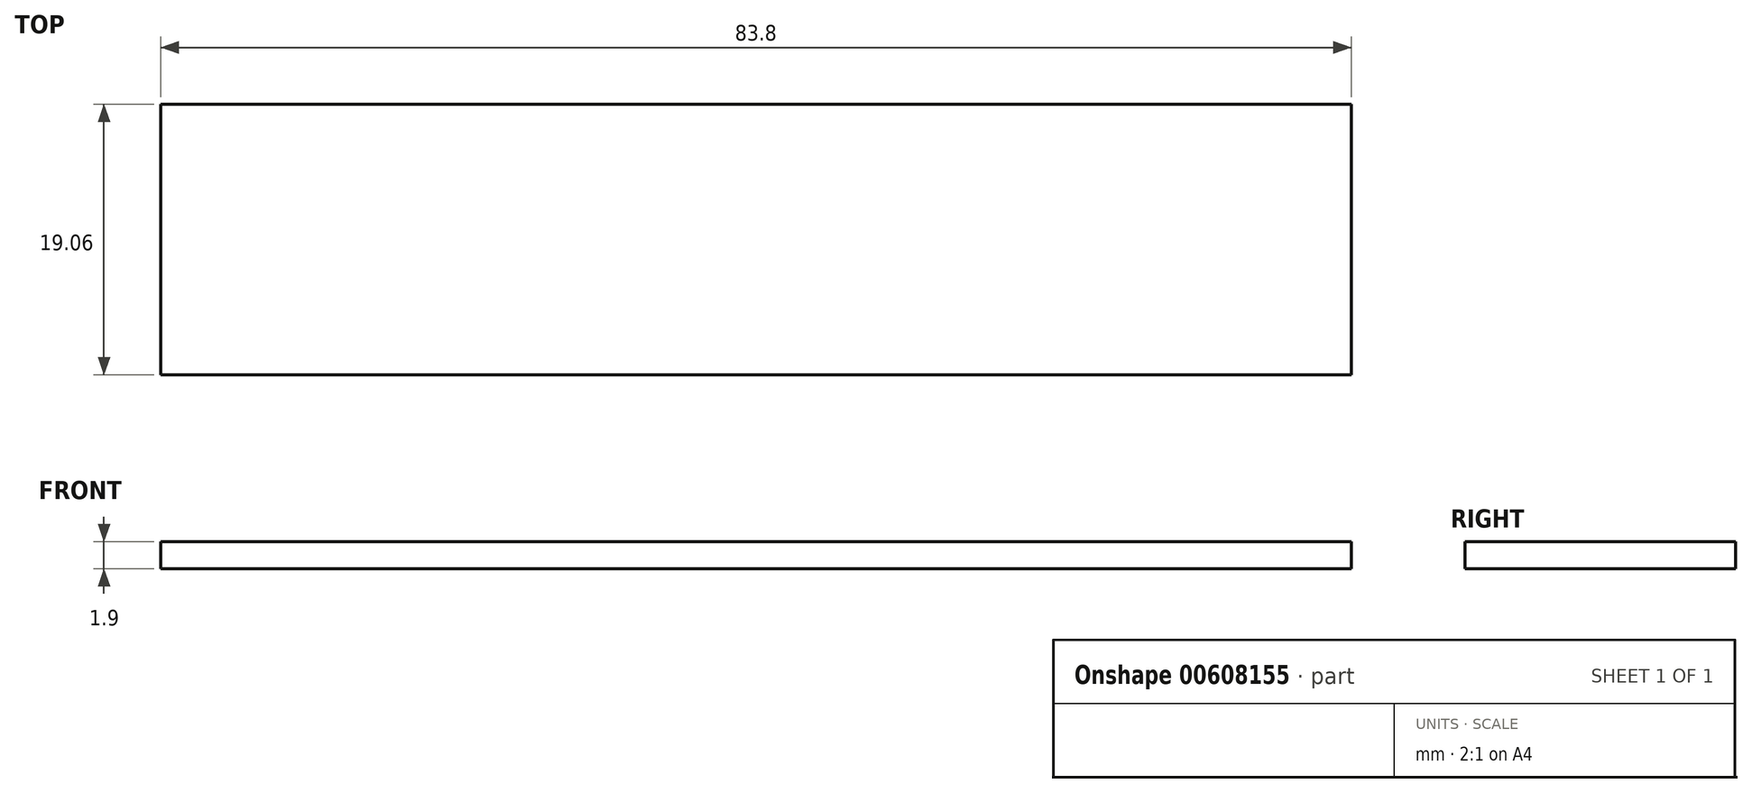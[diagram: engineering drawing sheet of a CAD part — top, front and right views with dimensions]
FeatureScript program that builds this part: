
annotation { "Feature Type Name" : "Feature", "Feature Type Description" : "" }
export const myFeature = defineFeature(function(context is Context, id is Id, definition is map)
    precondition{}
    {
        {
            var Q0;
            Q0=qCreatedBy(makeId("Top.planeOp"),FACE);
            var sketch = newSketch(context, id + "F0", { "sketchPlane" : qUnion([Q0])});
            skLineSegment(sketch, "E0.bottom", {"start": v(41.9, -9.53) * mm, "end": v(-41.9, -9.53) * mm});
            skLineSegment(sketch, "E0.top", {"start": v(41.9, 9.53) * mm, "end": v(-41.9, 9.53) * mm});
            skLineSegment(sketch, "E0.left", {"start": v(41.9, -9.53) * mm, "end": v(41.9, 9.52) * mm});
            skLineSegment(sketch, "E0.right", {"start": v(-41.9, -9.53) * mm, "end": v(-41.9, 9.52) * mm});
            skPoint(sketch, "E0.middle", {"position": v(0, 0) * mm});
            skSolve(sketch);
        }
        {
            var Q0;
            Q0 = qSketchRegion(id + "F0", true);
            extrude(context, id + "F1", {"entities" : qUnion([Q0]), "endBound" : BoundingType.SYMMETRIC, "depth" : 1.9 * mm, "offsetDistance" : 25 * mm});
        }
    });
